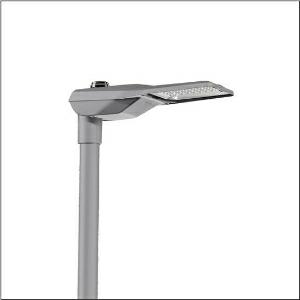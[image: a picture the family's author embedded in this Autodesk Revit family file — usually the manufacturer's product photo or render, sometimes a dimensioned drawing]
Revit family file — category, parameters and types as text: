
# Revit family: streetlight_sl_21_mini___stw1_0a_5xe6e47n08gb_debc
name_source: partatom
category: Lighting Fixtures
units: mm (PartAtom-declared; Revit-internal decimal feet)

## family parameters
Cut with Voids When Loaded = No
Host = Face
Light Source = No
Part Type = Normal
Room Calculation Point = No
Round Connector Dimension = Use Diameter
Shared = No

## types (1)
- --- (1 x LED, 6180 lm, 40.4 W, 4000K)
    Apparent Load = 40 VA
    CIE Flux Codes = 38 75 98 100 100
    Color Rendering = 70
    Color Temperature = 4000K
    Default Elevation = 1800 mm
    Description = Streetlight SL 21 mini, mast luminaire, primary light control with lens, of PMMA, primary optical cover: cover, of toughened safety glass, transparent, light distribution: STW1.0a, light emission: direct distribution, primary light characteristic: asymmetric, installation type: side-entry, LED, 3G 1.5mm², High Power LED, rated luminous flux: 6.180lm, luminous efficacy: 153lm/W, light colour: 740, colour temperature: 4000K, control gear: NEMA (7pin), control: overheat protection, pre-setting: linear dimming characteristic, constant luminous flux control, time-dependent luminous flux control, flexible luminous flux parameterisation, mains connection: 230..240V, AC, 50/60Hz, connection cable pre-assembled, cable length: 8,5m, wiring characteristics: H07RN-F, start of lifetime: 40W, end of service life: 41W, reduction: 19W, luminaire housing, of diecast aluminium (EN AC-44300), powder-coated, Siteco® metallic grey (DB 702S), corrosivity category C5 mid according to DIN EN ISO 12944, multi-level sealing system, sealing non-destructively replaceable, inclination adjustable: 0°, 5°, 10°, 15°, length: 628mm, width: 235mm, height: 110mm, spigot size: 42mm (side-entry), mounting height: 4..8m, protection rating (complete): IP66, insulation class (complete): insulation class I (protective earthing), certification: CE, ENEC, ENEC+, VDE, impact resistance: IK10, permissible operating ambient temperature for outdoor applications: -40..+50°C, standard-compliant lighting for roads and squares, packaging unit: 1 piece

Light Distribution: STW1.0a
    Height = 110 mm
    Lamp = 1 x LED
    Lamp Light Flux = 6180 lm
    Lamp Power = 40.4 W
    Lamp count = 1
    Length = 625 mm
    Luminous efficacy = 153 lm/W
    Manufacturer = Siteco
    ModVariant = No
    Model = 5XE6E47N08GB
    Number of Poles = 1
    OnlyDefault = Yes
    Power Factor = 1
    Product Name = Streetlight SL 21 mini | STW1.0a
    Product group = mast luminaire | pylon top
    ProductGroupID = 6100
    Protection Class = Protection class I
    Protection Degree = IP 66
    RLX_Detail_Level = 1
    RLX_Emergency_Light_Flux = 0 lm
    RLX_Emergency_Type = 0
    RLX_Emergency_Type_DB = No
    RlxData = <blob elided: 25885 chars, md5=e8655b9b>
    Socket = socket
    Standby Power = 0 W
    System Light Flux = 6180 lm
    System Power = 40 W
    Type Comments = factory setting: luminous flux: 100 % | dim-lin: 254 | 812 mA
    Type Image = l_1294379.jpg
    URL = http://relux.com
    VarID = @adj_157117
    Voltage = 0 V
    Weight = 0.00 kg
    Width = 234 mm

## geometry (parser evidence)
native form markers: Blend x4, Sweep x13
no freeform markers — native parametric forms only
